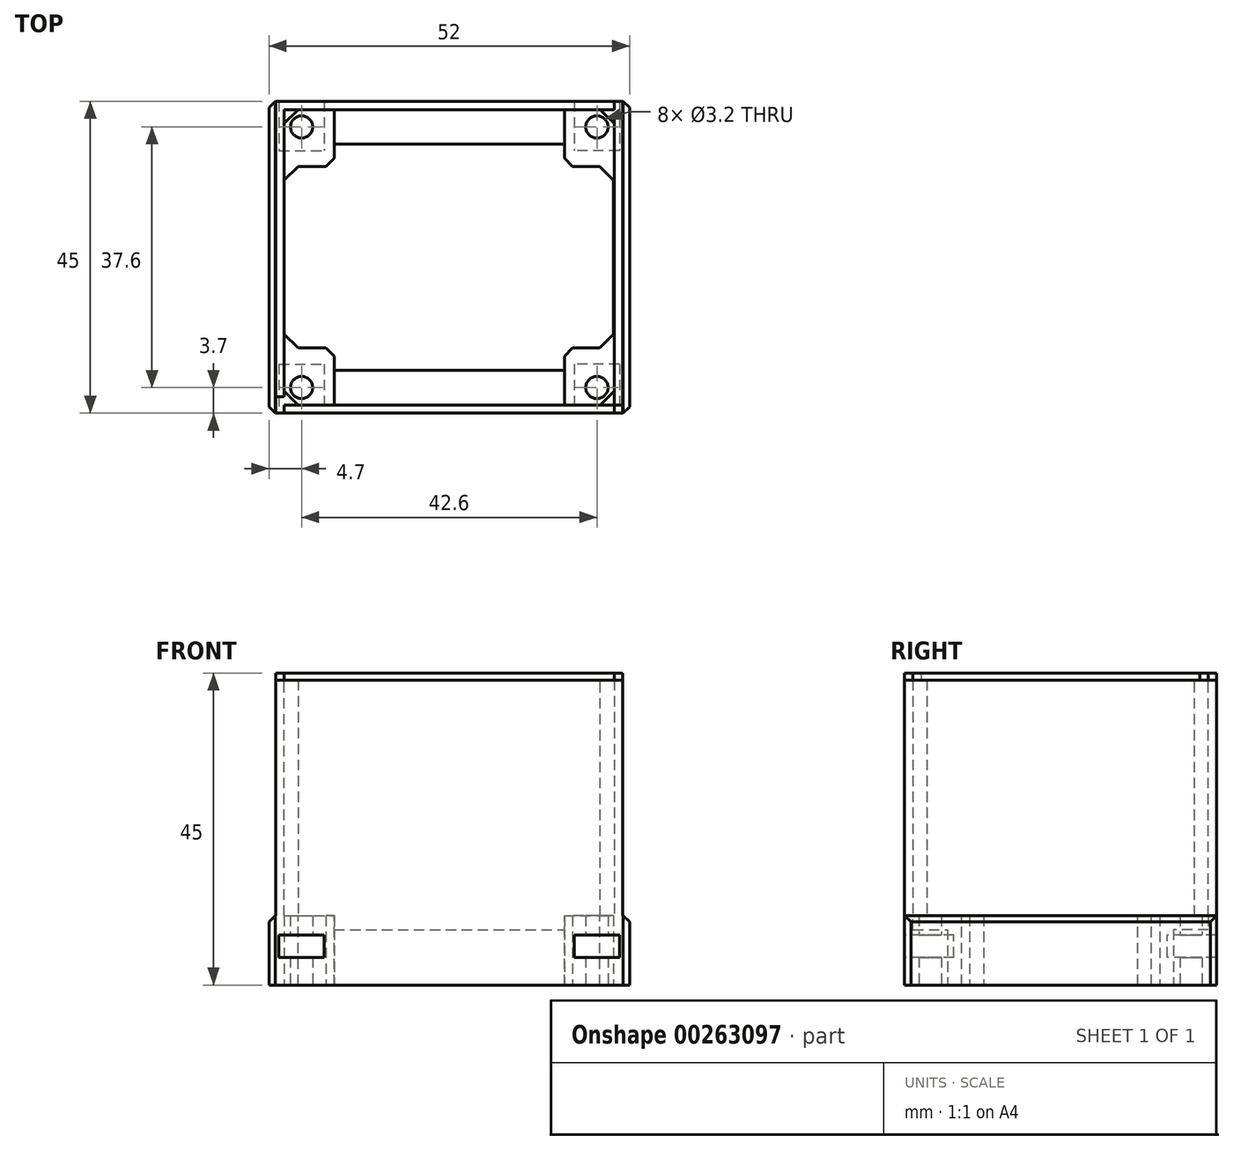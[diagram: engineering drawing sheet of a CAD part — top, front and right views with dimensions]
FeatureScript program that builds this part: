
annotation { "Feature Type Name" : "Feature", "Feature Type Description" : "" }
export const myFeature = defineFeature(function(context is Context, id is Id, definition is map)
    precondition{}
    {
        {
            var Q0;
            Q0=qCreatedBy(makeId("Top.planeOp"),FACE);
            var sketch = newSketch(context, id + "F0", { "sketchPlane" : qUnion([Q0])});
            skLineSegment(sketch, "E0.bottom", {"start": v(0, 45) * mm, "end": v(50, 45) * mm});
            skLineSegment(sketch, "E0.top", {"start": v(0, 0) * mm, "end": v(50, 0) * mm});
            skLineSegment(sketch, "E0.left", {"start": v(0, 45) * mm, "end": v(0, 0) * mm});
            skLineSegment(sketch, "E0.right", {"start": v(50, 45) * mm, "end": v(50, 0) * mm});
            skPoint(sketch, "E1.centerSnap0", {"position": v(0, 22.5) * mm});
            skLineSegment(sketch, "E2.bottom", {"start": v(1.2, 43.8) * mm, "end": v(48.8, 43.8) * mm});
            skLineSegment(sketch, "E2.top", {"start": v(1.2, 1.2) * mm, "end": v(48.8, 1.2) * mm});
            skLineSegment(sketch, "E2.right", {"start": v(48.8, 43.8) * mm, "end": v(48.8, 1.2) * mm});
            skLineSegment(sketch, "E3", {"start": v(1.2, 43.8) * mm, "end": v(1.2, 1.2) * mm});
            skLineSegment(sketch, "E4.bottom", {"start": v(0, 0) * mm, "end": v(1.2, 0) * mm});
            skLineSegment(sketch, "E4.top", {"start": v(0, 1.2) * mm, "end": v(1.2, 1.2) * mm});
            skLineSegment(sketch, "E4.left", {"start": v(0, 0) * mm, "end": v(0, 1.2) * mm});
            skLineSegment(sketch, "E4.right", {"start": v(1.2, 0) * mm, "end": v(1.2, 1.2) * mm});
            skLineSegment(sketch, "E5.bottom", {"start": v(1.2, 43.8) * mm, "end": v(0, 43.8) * mm});
            skLineSegment(sketch, "E5.top", {"start": v(1.2, 45) * mm, "end": v(0, 45) * mm});
            skLineSegment(sketch, "E5.left", {"start": v(1.2, 43.8) * mm, "end": v(1.2, 45) * mm});
            skLineSegment(sketch, "E5.right", {"start": v(0, 43.8) * mm, "end": v(0, 45) * mm});
            skLineSegment(sketch, "E6.bottom", {"start": v(50, 0) * mm, "end": v(48.8, 0) * mm});
            skLineSegment(sketch, "E6.top", {"start": v(50, 1.2) * mm, "end": v(48.8, 1.2) * mm});
            skLineSegment(sketch, "E6.left", {"start": v(50, 0) * mm, "end": v(50, 1.2) * mm});
            skLineSegment(sketch, "E6.right", {"start": v(48.8, 0) * mm, "end": v(48.8, 1.2) * mm});
            skLineSegment(sketch, "E7.bottom", {"start": v(48.8, 43.8) * mm, "end": v(50, 43.8) * mm});
            skLineSegment(sketch, "E7.top", {"start": v(48.8, 45) * mm, "end": v(50, 45) * mm});
            skLineSegment(sketch, "E7.left", {"start": v(48.8, 43.8) * mm, "end": v(48.8, 45) * mm});
            skLineSegment(sketch, "E7.right", {"start": v(50, 43.8) * mm, "end": v(50, 45) * mm});
            skSolve(sketch);
        }
        {
            var Q0;
            Q0=makeQuery(id+"F0.imprint","IMPRINT",FACE,{"disambiguationData":[TD([[makeQuery(id+"F0.imprint","IMPRINT",EDGE,{"derivedFrom":sQuery(id+"F0.wireOp",EDGE,"E0.bottom")}),-1.0]])]});
            var Q1;
            Q1=makeQuery(id+"F0.imprint","IMPRINT",FACE,{"disambiguationData":[TD([[makeQuery(id+"F0.imprint","IMPRINT",EDGE,{"derivedFrom":sQuery(id+"F0.wireOp",EDGE,"E7.bottom")}),1.0]])]});
            var Q2;
            Q2=makeQuery(id+"F0.imprint","IMPRINT",FACE,{"disambiguationData":[TD([[makeQuery(id+"F0.imprint","IMPRINT",EDGE,{"derivedFrom":sQuery(id+"F0.wireOp",EDGE,"E0.right")}),-1.0]])]});
            var Q3;
            Q3=makeQuery(id+"F0.imprint","IMPRINT",FACE,{"disambiguationData":[TD([[makeQuery(id+"F0.imprint","IMPRINT",EDGE,{"derivedFrom":sQuery(id+"F0.wireOp",EDGE,"E6.bottom")}),-1.0]])]});
            var Q4;
            Q4=makeQuery(id+"F0.imprint","IMPRINT",FACE,{"disambiguationData":[TD([[makeQuery(id+"F0.imprint","IMPRINT",EDGE,{"derivedFrom":sQuery(id+"F0.wireOp",EDGE,"E0.top")}),1.0]])]});
            var Q5;
            Q5=makeQuery(id+"F0.imprint","IMPRINT",FACE,{"disambiguationData":[TD([[makeQuery(id+"F0.imprint","IMPRINT",EDGE,{"derivedFrom":sQuery(id+"F0.wireOp",EDGE,"E4.bottom")}),1.0]])]});
            var Q6;
            Q6=makeQuery(id+"F0.imprint","IMPRINT",FACE,{"disambiguationData":[TD([[makeQuery(id+"F0.imprint","IMPRINT",EDGE,{"derivedFrom":sQuery(id+"F0.wireOp",EDGE,"E0.left")}),1.0]])]});
            var Q7;
            Q7=makeQuery(id+"F0.imprint","IMPRINT",FACE,{"disambiguationData":[TD([[makeQuery(id+"F0.imprint","IMPRINT",EDGE,{"derivedFrom":sQuery(id+"F0.wireOp",EDGE,"E5.bottom")}),-1.0]])]});
            extrude(context, id + "F1", {"entities" : qUnion([Q0, Q1, Q2, Q3, Q4, Q5, Q6, Q7]), "depth" : 44 * mm});
        }
        {
            var Q0;
            Q0=makeQuery(id+"F0.imprint","IMPRINT",FACE,{"disambiguationData":[TD([[makeQuery(id+"F0.imprint","IMPRINT",EDGE,{"derivedFrom":sQuery(id+"F0.wireOp",EDGE,"E2.bottom")}),-1.0]])]});
            var sketch = newSketch(context, id + "F2", { "sketchPlane" : qUnion([Q0])});
            skLineSegment(sketch, "E8.bottom", {"start": v(3.7, 41.3) * mm, "end": v(46.3, 41.3) * mm, "construction": true});
            skLineSegment(sketch, "E8.top", {"start": v(3.7, 3.7) * mm, "end": v(46.3, 3.7) * mm, "construction": true});
            skLineSegment(sketch, "E8.left", {"start": v(3.7, 41.3) * mm, "end": v(3.7, 3.7) * mm, "construction": true});
            skLineSegment(sketch, "E8.right", {"start": v(46.3, 41.3) * mm, "end": v(46.3, 3.7) * mm, "construction": true});
            skCircle(sketch, "E9", {"center": v(3.7, 41.3) * mm, "radius": 1.6 * mm});
            skCircle(sketch, "E10", {"center": v(46.3, 41.3) * mm, "radius": 1.6 * mm});
            skCircle(sketch, "E11", {"center": v(46.3, 3.7) * mm, "radius": 1.6 * mm});
            skCircle(sketch, "E12", {"center": v(3.7, 3.7) * mm, "radius": 1.6 * mm});
            skLineSegment(sketch, "E13.bottom", {"start": v(-1, 0) * mm, "end": v(8.4, 0) * mm});
            skLineSegment(sketch, "E13.top", {"start": v(-1, 9.4) * mm, "end": v(8.4, 9.4) * mm});
            skLineSegment(sketch, "E13.left", {"start": v(-1, 0) * mm, "end": v(-1, 9.4) * mm});
            skLineSegment(sketch, "E13.right", {"start": v(8.4, 0) * mm, "end": v(8.4, 9.4) * mm});
            skLineSegment(sketch, "E14", {"start": v(46.3, 22.5) * mm, "end": v(-11.44, 22.5) * mm, "construction": true});
            skLineSegment(sketch, "E15", {"start": v(25, 1.51) * mm, "end": v(25, 48.43) * mm, "construction": true});
            skPoint(sketch, "E15.startSnap0", {"position": v(25, 3.7) * mm});
            skPoint(sketch, "E15.endSnap0", {"position": v(25, 41.3) * mm});
            skLineSegment(sketch, "E16.MirrorCS", {"start": v(41.6, 0) * mm, "end": v(41.6, 9.4) * mm});
            skLineSegment(sketch, "E17.MirrorCS", {"start": v(51, 9.4) * mm, "end": v(41.6, 9.4) * mm});
            skLineSegment(sketch, "E18.MirrorCS", {"start": v(51, 0) * mm, "end": v(51, 9.4) * mm});
            skLineSegment(sketch, "E19.MirrorCS", {"start": v(51, 0) * mm, "end": v(41.6, 0) * mm});
            skLineSegment(sketch, "E20.MirrorCS", {"start": v(-1, 35.6) * mm, "end": v(8.4, 35.6) * mm});
            skLineSegment(sketch, "E21.MirrorCS", {"start": v(-1, 45) * mm, "end": v(-1, 35.6) * mm});
            skLineSegment(sketch, "E22.MirrorCS", {"start": v(-1, 45) * mm, "end": v(8.4, 45) * mm});
            skLineSegment(sketch, "E23.MirrorCS", {"start": v(8.4, 45) * mm, "end": v(8.4, 35.6) * mm});
            skLineSegment(sketch, "E24.MirrorCS", {"start": v(51, 35.6) * mm, "end": v(41.6, 35.6) * mm});
            skLineSegment(sketch, "E25.MirrorCS", {"start": v(41.6, 45) * mm, "end": v(41.6, 35.6) * mm});
            skLineSegment(sketch, "E26.MirrorCS", {"start": v(51, 45) * mm, "end": v(41.6, 45) * mm});
            skLineSegment(sketch, "E27.MirrorCS", {"start": v(51, 45) * mm, "end": v(51, 35.6) * mm});
            skLineSegment(sketch, "E28.bottom", {"start": v(51, 9.4) * mm, "end": v(48.7, 9.4) * mm});
            skLineSegment(sketch, "E28.top", {"start": v(51, 35.6) * mm, "end": v(48.7, 35.6) * mm});
            skLineSegment(sketch, "E28.left", {"start": v(51, 9.4) * mm, "end": v(51, 35.6) * mm});
            skLineSegment(sketch, "E28.right", {"start": v(48.7, 9.4) * mm, "end": v(48.7, 35.6) * mm});
            skLineSegment(sketch, "E29.bottom", {"start": v(-1, 35.6) * mm, "end": v(0.48, 35.6) * mm});
            skLineSegment(sketch, "E29.top", {"start": v(-1, 9.4) * mm, "end": v(0.48, 9.4) * mm});
            skLineSegment(sketch, "E29.left", {"start": v(-1, 35.6) * mm, "end": v(-1, 9.4) * mm});
            skLineSegment(sketch, "E29.right", {"start": v(0.48, 35.6) * mm, "end": v(0.48, 9.4) * mm});
            skSolve(sketch);
        }
        {
            var Q0;
            Q0 = qSketchRegion(id + "F2", true);
            extrude(context, id + "F3", {"entities" : qUnion([Q0]), "operationType" : NewBodyOperationType.ADD, "depth" : 10 * mm});
        }
        {
            var Q0;
            Q0=makeQuery(id+"F3.boolean.opBoolean","MERGE",FACE,{"derivedFrom":[makeQuery(id+"F1.opExtrude","SWEPT_FACE",FACE,{"disambiguationData":[OSD([sQuery(id+"F0.wireOp",EDGE,"E0.top"),sQuery(id+"F0.wireOp",EDGE,"E4.bottom"),sQuery(id+"F0.wireOp",EDGE,"E6.bottom")])]}),makeQuery(id+"F3.opExtrude","SWEPT_FACE",FACE,{"disambiguationData":[OSD([sQuery(id+"F2.wireOp",EDGE,"E13.bottom")])]}),makeQuery(id+"F3.opExtrude","SWEPT_FACE",FACE,{"disambiguationData":[OSD([sQuery(id+"F2.wireOp",EDGE,"E19.MirrorCS")])]})]});
            var sketch = newSketch(context, id + "F4", { "sketchPlane" : qUnion([Q0])});
            skLineSegment(sketch, "E30.bottom", {"start": v(0.45, 4) * mm, "end": v(6.95, 4) * mm});
            skLineSegment(sketch, "E30.top", {"start": v(0.45, 7.2) * mm, "end": v(6.95, 7.2) * mm});
            skLineSegment(sketch, "E30.left", {"start": v(0.45, 4) * mm, "end": v(0.45, 7.2) * mm});
            skLineSegment(sketch, "E30.right", {"start": v(6.95, 4) * mm, "end": v(6.95, 7.2) * mm});
            skLineSegment(sketch, "E31", {"start": v(25, 0) * mm, "end": v(25, 25.68) * mm, "construction": true});
            skLineSegment(sketch, "E32.MirrorCS", {"start": v(49.55, 7.2) * mm, "end": v(43.05, 7.2) * mm});
            skLineSegment(sketch, "E33.MirrorCS", {"start": v(49.55, 4) * mm, "end": v(49.55, 7.2) * mm});
            skLineSegment(sketch, "E34.MirrorCS", {"start": v(49.55, 4) * mm, "end": v(43.05, 4) * mm});
            skLineSegment(sketch, "E35.MirrorCS", {"start": v(43.05, 4) * mm, "end": v(43.05, 7.2) * mm});
            skSolve(sketch);
        }
        {
            var Q0;
            Q0=makeQuery(id+"F4.imprint","IMPRINT",FACE,{"disambiguationData":[TD([[makeQuery(id+"F4.imprint","IMPRINT",EDGE,{"derivedFrom":sQuery(id+"F4.wireOp",EDGE,"E30.bottom")}),1.0]])]});
            var Q1;
            Q1=makeQuery(id+"F4.imprint","IMPRINT",FACE,{"disambiguationData":[TD([[makeQuery(id+"F4.imprint","IMPRINT",EDGE,{"derivedFrom":sQuery(id+"F4.wireOp",EDGE,"E32.MirrorCS")}),1.0]])]});
            extrude(context, id + "F5", {"entities" : qUnion([Q0, Q1]), "operationType" : NewBodyOperationType.REMOVE, "oppositeDirection" : true, "depth" : 7.1 * mm});
        }
        {
            var Q0;
            Q0=makeQuery(id+"F4.imprint","IMPRINT",FACE,{"disambiguationData":[TD([[makeQuery(id+"F4.imprint","IMPRINT",EDGE,{"derivedFrom":sQuery(id+"F4.wireOp",EDGE,"E30.bottom")}),1.0]])]});
            var Q1;
            Q1=makeQuery(id+"F4.imprint","IMPRINT",FACE,{"disambiguationData":[TD([[makeQuery(id+"F4.imprint","IMPRINT",EDGE,{"derivedFrom":sQuery(id+"F4.wireOp",EDGE,"E32.MirrorCS")}),1.0]])]});
            extrude(context, id + "F6", {"entities" : qUnion([Q0, Q1]), "operationType" : NewBodyOperationType.REMOVE, "oppositeDirection" : true, "depth" : 45 * mm, "hasSecondDirection" : true, "secondDirectionOppositeDirection" : true, "secondDirectionDepth" : 37.9 * mm});
        }
        {
            var Q0;
            Q0=makeQuery(id+"F3.opExtrude","SWEPT_EDGE",EDGE,{"disambiguationData":[OSD([sQuery(id+"F2.wireOp",EDGE,"E21.MirrorCS"),sQuery(id+"F2.wireOp",EDGE,"E22.MirrorCS")])]});
            var Q1;
            Q1=makeQuery(id+"F3.opExtrude","CAP_EDGE",EDGE,{"disambiguationData":[OSD([sQuery(id+"F2.wireOp",EDGE,"E13.left"),sQuery(id+"F2.wireOp",EDGE,"E21.MirrorCS"),sQuery(id+"F2.wireOp",EDGE,"E29.left")])],"isStart":false});
            var Q2;
            Q2=makeQuery(id+"F3.opExtrude","CAP_EDGE",EDGE,{"disambiguationData":[OSD([sQuery(id+"F2.wireOp",EDGE,"E13.left"),sQuery(id+"F2.wireOp",EDGE,"E21.MirrorCS"),sQuery(id+"F2.wireOp",EDGE,"E29.left")])],"isStart":false});
            var Q3;
            Q3=makeQuery(id+"F3.opExtrude","CAP_EDGE",EDGE,{"disambiguationData":[OSD([sQuery(id+"F2.wireOp",EDGE,"E18.MirrorCS"),sQuery(id+"F2.wireOp",EDGE,"E27.MirrorCS"),sQuery(id+"F2.wireOp",EDGE,"E28.left")])],"isStart":false});
            var Q4;
            Q4=makeQuery(id+"F3.opExtrude","CAP_EDGE",EDGE,{"disambiguationData":[OSD([sQuery(id+"F2.wireOp",EDGE,"E18.MirrorCS"),sQuery(id+"F2.wireOp",EDGE,"E27.MirrorCS"),sQuery(id+"F2.wireOp",EDGE,"E28.left")])],"isStart":false});
            var Q5;
            Q5=makeQuery(id+"F3.opExtrude","SWEPT_EDGE",EDGE,{"disambiguationData":[OSD([sQuery(id+"F2.wireOp",EDGE,"E13.bottom"),sQuery(id+"F2.wireOp",EDGE,"E13.left")])]});
            var Q6;
            Q6=makeQuery(id+"F3.opExtrude","SWEPT_EDGE",EDGE,{"disambiguationData":[OSD([sQuery(id+"F2.wireOp",EDGE,"E18.MirrorCS"),sQuery(id+"F2.wireOp",EDGE,"E19.MirrorCS")])]});
            var Q7;
            Q7=makeQuery(id+"F3.opExtrude","SWEPT_EDGE",EDGE,{"disambiguationData":[OSD([sQuery(id+"F2.wireOp",EDGE,"E26.MirrorCS"),sQuery(id+"F2.wireOp",EDGE,"E27.MirrorCS")])]});
            var Q8;
            Q8=makeQuery(id+"F3.opExtrude","SWEPT_EDGE",EDGE,{"disambiguationData":[OSD([sQuery(id+"F2.wireOp",EDGE,"E26.MirrorCS"),sQuery(id+"F2.wireOp",EDGE,"E27.MirrorCS")])]});
            var Q9;
            Q9=makeQuery(id+"F3.opExtrude","SWEPT_EDGE",EDGE,{"disambiguationData":[OSD([sQuery(id+"F2.wireOp",EDGE,"E18.MirrorCS"),sQuery(id+"F2.wireOp",EDGE,"E19.MirrorCS")])]});
            var Q10;
            Q10=makeQuery(id+"F3.opExtrude","SWEPT_EDGE",EDGE,{"disambiguationData":[OSD([sQuery(id+"F2.wireOp",EDGE,"E13.bottom"),sQuery(id+"F2.wireOp",EDGE,"E13.left")])]});
            chamfer(context, id + "F7", {"entities" : qUnion([Q0, Q1, Q2, Q3, Q4, Q5, Q6, Q7, Q8, Q9, Q10]), "width" : 0.9 * mm, "tangentPropagation" : true});
        }
        {
            var Q0;
            Q0=makeQuery(id+"F1.opExtrude","CAP_FACE",FACE,{"disambiguationData":[OSD([sQuery(id+"F0.wireOp",EDGE,"E0.bottom"),sQuery(id+"F0.wireOp",EDGE,"E0.top"),sQuery(id+"F0.wireOp",EDGE,"E0.left"),sQuery(id+"F0.wireOp",EDGE,"E0.right"),sQuery(id+"F0.wireOp",EDGE,"E2.bottom"),sQuery(id+"F0.wireOp",EDGE,"E2.top"),sQuery(id+"F0.wireOp",EDGE,"E2.right"),sQuery(id+"F0.wireOp",EDGE,"E3"),sQuery(id+"F0.wireOp",EDGE,"E4.bottom"),sQuery(id+"F0.wireOp",EDGE,"E4.left"),sQuery(id+"F0.wireOp",EDGE,"E5.top"),sQuery(id+"F0.wireOp",EDGE,"E5.right"),sQuery(id+"F0.wireOp",EDGE,"E6.bottom"),sQuery(id+"F0.wireOp",EDGE,"E6.left"),sQuery(id+"F0.wireOp",EDGE,"E7.top"),sQuery(id+"F0.wireOp",EDGE,"E7.right")])],"isStart":false});
            var sketch = newSketch(context, id + "F8", { "sketchPlane" : qUnion([Q0])});
            skLineSegment(sketch, "E36.bottom", {"start": v(0, 45) * mm, "end": v(1.2, 45) * mm});
            skLineSegment(sketch, "E36.top", {"start": v(0, 43.8) * mm, "end": v(1.2, 43.8) * mm});
            skLineSegment(sketch, "E36.left", {"start": v(0, 45) * mm, "end": v(0, 43.8) * mm});
            skLineSegment(sketch, "E36.right", {"start": v(1.2, 45) * mm, "end": v(1.2, 43.8) * mm});
            skLineSegment(sketch, "E37.bottom", {"start": v(1.2, 1.2) * mm, "end": v(0, 1.2) * mm});
            skLineSegment(sketch, "E37.top", {"start": v(1.2, 0) * mm, "end": v(0, 0) * mm});
            skLineSegment(sketch, "E37.left", {"start": v(1.2, 1.2) * mm, "end": v(1.2, 0) * mm});
            skLineSegment(sketch, "E37.right", {"start": v(0, 1.2) * mm, "end": v(0, 0) * mm});
            skLineSegment(sketch, "E38.bottom", {"start": v(48.8, 1.2) * mm, "end": v(50, 1.2) * mm});
            skLineSegment(sketch, "E38.top", {"start": v(48.8, 0) * mm, "end": v(50, 0) * mm});
            skLineSegment(sketch, "E38.left", {"start": v(48.8, 1.2) * mm, "end": v(48.8, 0) * mm});
            skLineSegment(sketch, "E38.right", {"start": v(50, 1.2) * mm, "end": v(50, 0) * mm});
            skLineSegment(sketch, "E39.bottom", {"start": v(48.8, 43.8) * mm, "end": v(50, 43.8) * mm});
            skLineSegment(sketch, "E39.top", {"start": v(48.8, 45) * mm, "end": v(50, 45) * mm});
            skLineSegment(sketch, "E39.left", {"start": v(48.8, 43.8) * mm, "end": v(48.8, 45) * mm});
            skLineSegment(sketch, "E39.right", {"start": v(50, 43.8) * mm, "end": v(50, 45) * mm});
            skLineSegment(sketch, "E40.bottom", {"start": v(1.2, 45) * mm, "end": v(48.8, 45) * mm});
            skLineSegment(sketch, "E40.top", {"start": v(1.2, 43.8) * mm, "end": v(48.8, 43.8) * mm});
            skLineSegment(sketch, "E40.right", {"start": v(48.8, 45) * mm, "end": v(48.8, 43.8) * mm});
            skLineSegment(sketch, "E41.bottom", {"start": v(50, 42.6) * mm, "end": v(48.8, 42.6) * mm});
            skLineSegment(sketch, "E41.top", {"start": v(50, 1.2) * mm, "end": v(48.8, 1.2) * mm});
            skLineSegment(sketch, "E41.left", {"start": v(50, 42.6) * mm, "end": v(50, 1.2) * mm});
            skLineSegment(sketch, "E41.right", {"start": v(48.8, 42.6) * mm, "end": v(48.8, 1.2) * mm});
            skLineSegment(sketch, "E42.bottom", {"start": v(48.8, 1.2) * mm, "end": v(1.2, 1.2) * mm});
            skLineSegment(sketch, "E42.top", {"start": v(48.8, 0) * mm, "end": v(1.2, 0) * mm});
            skLineSegment(sketch, "E43.bottom", {"start": v(1.2, 2.4) * mm, "end": v(0, 2.4) * mm});
            skLineSegment(sketch, "E43.top", {"start": v(1.2, 43.8) * mm, "end": v(0, 43.8) * mm});
            skLineSegment(sketch, "E43.left", {"start": v(1.2, 1.2) * mm, "end": v(1.2, 43.8) * mm});
            skLineSegment(sketch, "E43.right", {"start": v(0, 2.4) * mm, "end": v(0, 43.8) * mm});
            skSolve(sketch);
        }
        {
            var Q0;
            Q0=makeQuery(id+"F8.imprint","IMPRINT",FACE,{"disambiguationData":[TD([[makeQuery(id+"F8.imprint","IMPRINT",EDGE,{"derivedFrom":sQuery(id+"F8.wireOp",EDGE,"E40.bottom")}),-1.0]])]});
            var Q1;
            Q1=makeQuery(id+"F8.imprint","IMPRINT",FACE,{"disambiguationData":[TD([[makeQuery(id+"F8.imprint","IMPRINT",EDGE,{"derivedFrom":sQuery(id+"F8.wireOp",EDGE,"E41.bottom")}),1.0]])]});
            var Q2;
            Q2=makeQuery(id+"F8.imprint","IMPRINT",FACE,{"disambiguationData":[TD([[makeQuery(id+"F8.imprint","IMPRINT",EDGE,{"derivedFrom":sQuery(id+"F8.wireOp",EDGE,"E42.bottom")}),-1.0]])]});
            var Q3;
            Q3=makeQuery(id+"F8.imprint","IMPRINT",FACE,{"disambiguationData":[TD([[makeQuery(id+"F8.imprint","IMPRINT",EDGE,{"derivedFrom":sQuery(id+"F8.wireOp",EDGE,"E43.bottom")}),-1.0]])]});
            var Q4;
            Q4=makeQuery(id+"F8.imprint","IMPRINT",FACE,{"disambiguationData":[TD([[makeQuery(id+"F8.imprint","IMPRINT",EDGE,{"derivedFrom":sQuery(id+"F8.wireOp",EDGE,"E38.top")}),-1.0]])]});
            var Q5;
            Q5=makeQuery(id+"F8.imprint","IMPRINT",FACE,{"disambiguationData":[TD([[makeQuery(id+"F8.imprint","IMPRINT",EDGE,{"derivedFrom":sQuery(id+"F8.wireOp",EDGE,"E36.bottom")}),-1.0]])]});
            extrude(context, id + "F9", {"entities" : qUnion([Q0, Q1, Q2, Q3, Q4, Q5]), "depth" : 1 * mm});
        }
        {
            var Q0;
            Q0=makeQuery(id+"F0.imprint","IMPRINT",FACE,{"disambiguationData":[TD([[makeQuery(id+"F0.imprint","IMPRINT",EDGE,{"derivedFrom":sQuery(id+"F0.wireOp",EDGE,"E2.bottom")}),-1.0]])]});
            var sketch = newSketch(context, id + "F10", { "sketchPlane" : qUnion([Q0])});
            skLineSegment(sketch, "E44.bottom", {"start": v(41.6, 43.8) * mm, "end": v(8.4, 43.8) * mm});
            skLineSegment(sketch, "E44.top", {"start": v(41.6, 38.8) * mm, "end": v(8.4, 38.8) * mm});
            skLineSegment(sketch, "E44.left", {"start": v(41.6, 43.8) * mm, "end": v(41.6, 38.8) * mm});
            skLineSegment(sketch, "E44.right", {"start": v(8.4, 43.8) * mm, "end": v(8.4, 38.8) * mm});
            skLineSegment(sketch, "E45.bottom", {"start": v(41.6, 1.2) * mm, "end": v(8.4, 1.2) * mm});
            skLineSegment(sketch, "E45.top", {"start": v(41.6, 6.2) * mm, "end": v(8.4, 6.2) * mm});
            skLineSegment(sketch, "E45.left", {"start": v(41.6, 1.2) * mm, "end": v(41.6, 6.2) * mm});
            skLineSegment(sketch, "E45.right", {"start": v(8.4, 1.2) * mm, "end": v(8.4, 6.2) * mm});
            skSolve(sketch);
        }
        {
            var Q0;
            Q0 = qSketchRegion(id + "F10", true);
            extrude(context, id + "F11", {"entities" : qUnion([Q0]), "operationType" : NewBodyOperationType.ADD, "depth" : 8 * mm});
        }
        {
            var Q0;
            Q0=makeQuery(id+"F11.opExtrude","CAP_EDGE",EDGE,{"disambiguationData":[OSD([sQuery(id+"F10.wireOp",EDGE,"E44.right")])],"isStart":false});
            var Q1;
            Q1=makeQuery(id+"F11.opExtrude","CAP_EDGE",EDGE,{"disambiguationData":[OSD([sQuery(id+"F10.wireOp",EDGE,"E44.left")])],"isStart":false});
            var Q2;
            Q2=makeQuery(id+"F11.opExtrude","SWEPT_EDGE",EDGE,{"disambiguationData":[OSD([sQuery(id+"F10.wireOp",EDGE,"E44.top"),sQuery(id+"F10.wireOp",EDGE,"E44.left")])]});
            var Q3;
            Q3=makeQuery(id+"F11.opExtrude","SWEPT_EDGE",EDGE,{"disambiguationData":[OSD([sQuery(id+"F10.wireOp",EDGE,"E44.top"),sQuery(id+"F10.wireOp",EDGE,"E44.right")])]});
            var Q4;
            Q4=makeQuery(id+"F11.opExtrude","SWEPT_EDGE",EDGE,{"disambiguationData":[OSD([sQuery(id+"F10.wireOp",EDGE,"E45.top"),sQuery(id+"F10.wireOp",EDGE,"E45.left")])]});
            var Q5;
            Q5=makeQuery(id+"F11.opExtrude","CAP_EDGE",EDGE,{"disambiguationData":[OSD([sQuery(id+"F10.wireOp",EDGE,"E45.left")])],"isStart":false});
            var Q6;
            Q6=makeQuery(id+"F11.opExtrude","CAP_EDGE",EDGE,{"disambiguationData":[OSD([sQuery(id+"F10.wireOp",EDGE,"E45.right")])],"isStart":false});
            var Q7;
            Q7=makeQuery(id+"F11.opExtrude","SWEPT_EDGE",EDGE,{"disambiguationData":[OSD([sQuery(id+"F10.wireOp",EDGE,"E45.top"),sQuery(id+"F10.wireOp",EDGE,"E45.right")])]});
            var Q8;
            Q8=makeQuery(id+"F3.boolean.opBoolean","INTERSECT",EDGE,{"derivedFrom":[makeQuery(id+"F1.opExtrude","SWEPT_FACE",FACE,{"disambiguationData":[OSD([sQuery(id+"F0.wireOp",EDGE,"E3")])]}),makeQuery(id+"F3.opExtrude","SWEPT_FACE",FACE,{"disambiguationData":[OSD([sQuery(id+"F2.wireOp",EDGE,"E20.MirrorCS")])]})]});
            var Q9;
            Q9=makeQuery(id+"F3.opExtrude","SWEPT_EDGE",EDGE,{"disambiguationData":[OSD([sQuery(id+"F2.wireOp",EDGE,"E24.MirrorCS"),sQuery(id+"F2.wireOp",EDGE,"E28.top"),sQuery(id+"F2.wireOp",EDGE,"E28.right")])]});
            var Q10;
            Q10=makeQuery(id+"F3.opExtrude","SWEPT_EDGE",EDGE,{"disambiguationData":[OSD([sQuery(id+"F2.wireOp",EDGE,"E17.MirrorCS"),sQuery(id+"F2.wireOp",EDGE,"E28.bottom"),sQuery(id+"F2.wireOp",EDGE,"E28.right")])]});
            var Q11;
            Q11=makeQuery(id+"F3.boolean.opBoolean","INTERSECT",EDGE,{"derivedFrom":[makeQuery(id+"F1.opExtrude","SWEPT_FACE",FACE,{"disambiguationData":[OSD([sQuery(id+"F0.wireOp",EDGE,"E3")])]}),makeQuery(id+"F3.opExtrude","SWEPT_FACE",FACE,{"disambiguationData":[OSD([sQuery(id+"F2.wireOp",EDGE,"E13.top")])]})]});
            chamfer(context, id + "F12", {"entities" : qUnion([Q0, Q1, Q2, Q3, Q4, Q5, Q6, Q7, Q8, Q9, Q10, Q11]), "width" : 2 * mm, "tangentPropagation" : true});
        }
        {
            var Q0;
            Q0=makeQuery(id+"F1.opExtrude","SWEPT_EDGE",EDGE,{"disambiguationData":[OSD([sQuery(id+"F0.wireOp",EDGE,"E2.bottom"),sQuery(id+"F0.wireOp",EDGE,"E2.right"),sQuery(id+"F0.wireOp",EDGE,"E7.bottom"),sQuery(id+"F0.wireOp",EDGE,"E7.left")])]});
            var Q1;
            Q1=makeQuery(id+"F1.opExtrude","SWEPT_EDGE",EDGE,{"disambiguationData":[OSD([sQuery(id+"F0.wireOp",EDGE,"E2.bottom"),sQuery(id+"F0.wireOp",EDGE,"E3"),sQuery(id+"F0.wireOp",EDGE,"E5.bottom"),sQuery(id+"F0.wireOp",EDGE,"E5.left")])]});
            var Q2;
            Q2=makeQuery(id+"F1.opExtrude","SWEPT_EDGE",EDGE,{"disambiguationData":[OSD([sQuery(id+"F0.wireOp",EDGE,"E2.top"),sQuery(id+"F0.wireOp",EDGE,"E3"),sQuery(id+"F0.wireOp",EDGE,"E4.top"),sQuery(id+"F0.wireOp",EDGE,"E4.right")])]});
            var Q3;
            Q3=makeQuery(id+"F1.opExtrude","SWEPT_EDGE",EDGE,{"disambiguationData":[OSD([sQuery(id+"F0.wireOp",EDGE,"E2.top"),sQuery(id+"F0.wireOp",EDGE,"E2.right"),sQuery(id+"F0.wireOp",EDGE,"E6.top"),sQuery(id+"F0.wireOp",EDGE,"E6.right")])]});
            chamfer(context, id + "F13", {"entities" : qUnion([Q0, Q1, Q2, Q3]), "width" : 2 * mm, "tangentPropagation" : true});
        }
        {
            var Q0;
            Q0=makeQuery(id+"F3.opExtrude","SWEPT_EDGE",EDGE,{"disambiguationData":[OSD([sQuery(id+"F2.wireOp",EDGE,"E20.MirrorCS"),sQuery(id+"F2.wireOp",EDGE,"E23.MirrorCS")])]});
            var Q1;
            Q1=makeQuery(id+"F3.opExtrude","SWEPT_EDGE",EDGE,{"disambiguationData":[OSD([sQuery(id+"F2.wireOp",EDGE,"E24.MirrorCS"),sQuery(id+"F2.wireOp",EDGE,"E25.MirrorCS")])]});
            var Q2;
            Q2=makeQuery(id+"F3.opExtrude","SWEPT_EDGE",EDGE,{"disambiguationData":[OSD([sQuery(id+"F2.wireOp",EDGE,"E16.MirrorCS"),sQuery(id+"F2.wireOp",EDGE,"E17.MirrorCS")])]});
            var Q3;
            Q3=makeQuery(id+"F3.opExtrude","SWEPT_EDGE",EDGE,{"disambiguationData":[OSD([sQuery(id+"F2.wireOp",EDGE,"E13.top"),sQuery(id+"F2.wireOp",EDGE,"E13.right")])]});
            chamfer(context, id + "F14", {"entities" : qUnion([Q0, Q1, Q2, Q3]), "width" : 1.2 * mm, "tangentPropagation" : true});
        }
    });
